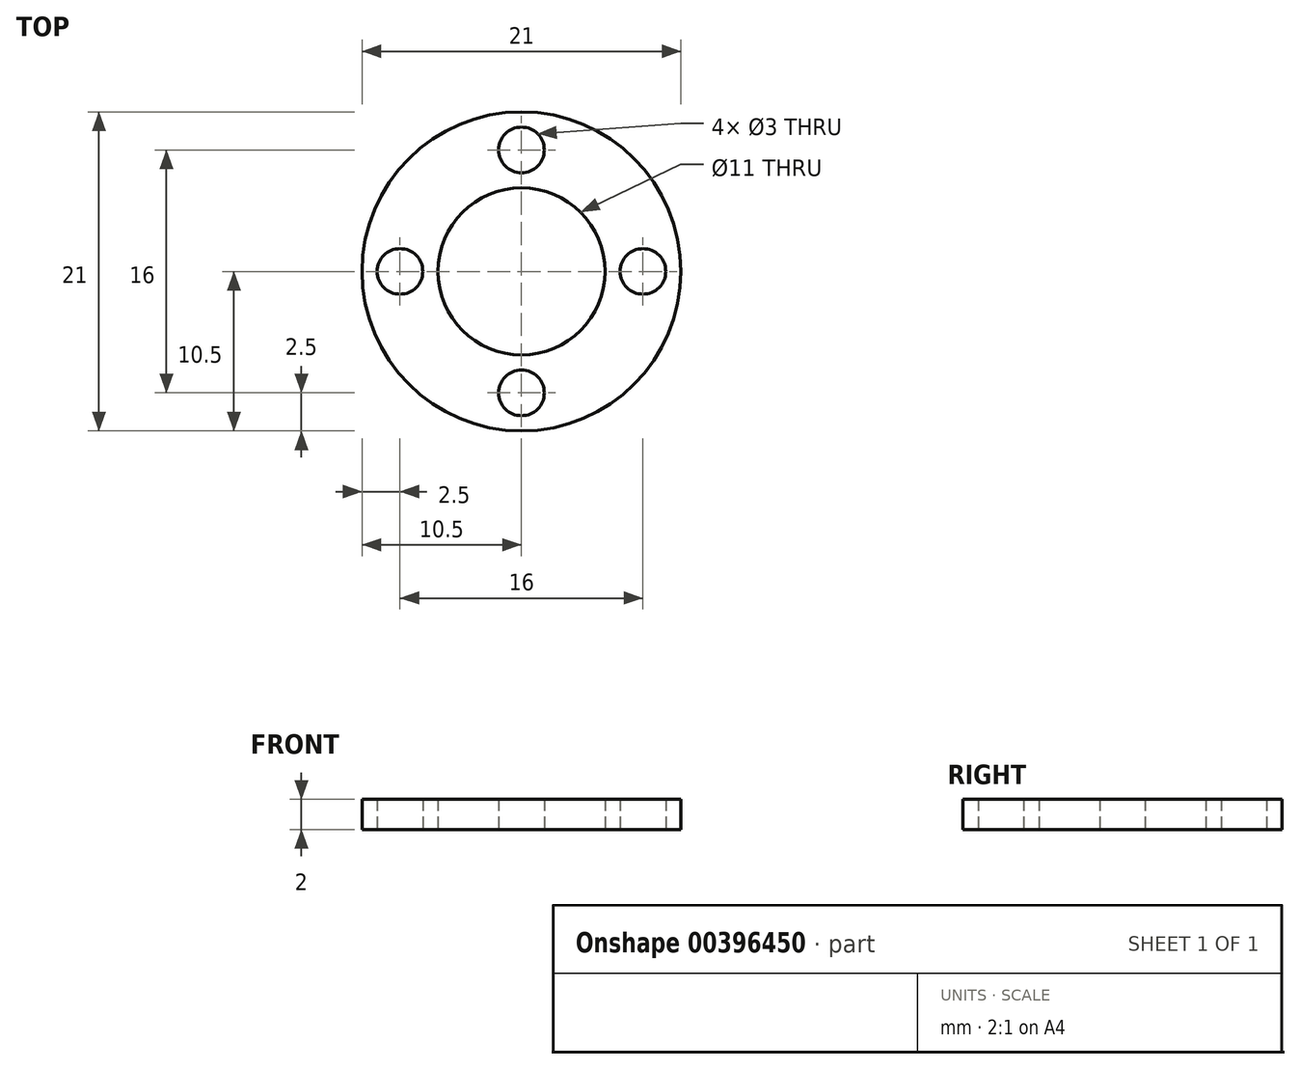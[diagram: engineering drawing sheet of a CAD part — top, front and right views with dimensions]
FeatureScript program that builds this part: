
annotation { "Feature Type Name" : "Feature", "Feature Type Description" : "" }
export const myFeature = defineFeature(function(context is Context, id is Id, definition is map)
    precondition{}
    {
        {
            var Q0;
            Q0=qCreatedBy(makeId("Top.planeOp"),FACE);
            var sketch = newSketch(context, id + "F0", { "sketchPlane" : qUnion([Q0])});
            skCircle(sketch, "E0", {"center": v(0, 0) * mm, "radius": 10.5 * mm});
            skCircle(sketch, "E1", {"center": v(0, 0) * mm, "radius": 5.5 * mm});
            skLineSegment(sketch, "E2", {"start": v(0, 0) * mm, "end": v(0, 8) * mm});
            skLineSegment(sketch, "E3", {"start": v(0, 8) * mm, "end": v(0, -8) * mm});
            skLineSegment(sketch, "E4", {"start": v(0, 0) * mm, "end": v(8, 0) * mm});
            skLineSegment(sketch, "E5", {"start": v(8, 0) * mm, "end": v(-8, 0) * mm});
            skPoint(sketch, "E5.endSnap0", {"position": v(4, 0) * mm});
            skCircle(sketch, "E6", {"center": v(-8, 0) * mm, "radius": 1.5 * mm});
            skCircle(sketch, "E7", {"center": v(0, 8) * mm, "radius": 1.5 * mm});
            skCircle(sketch, "E8", {"center": v(8, 0) * mm, "radius": 1.5 * mm});
            skCircle(sketch, "E9", {"center": v(0, -8) * mm, "radius": 1.5 * mm});
            skSolve(sketch);
        }
        {
            var Q0;
            Q0=makeQuery(id+"F0.imprint","IMPRINT",FACE,{"disambiguationData":[TD([[makeQuery(id+"F0.imprint","IMPRINT",EDGE,{"derivedFrom":sQuery(id+"F0.wireOp",EDGE,"E0")}),1.0]])]});
            extrude(context, id + "F1", {"entities" : qUnion([Q0]), "depth" : 2 * mm});
        }
    });
